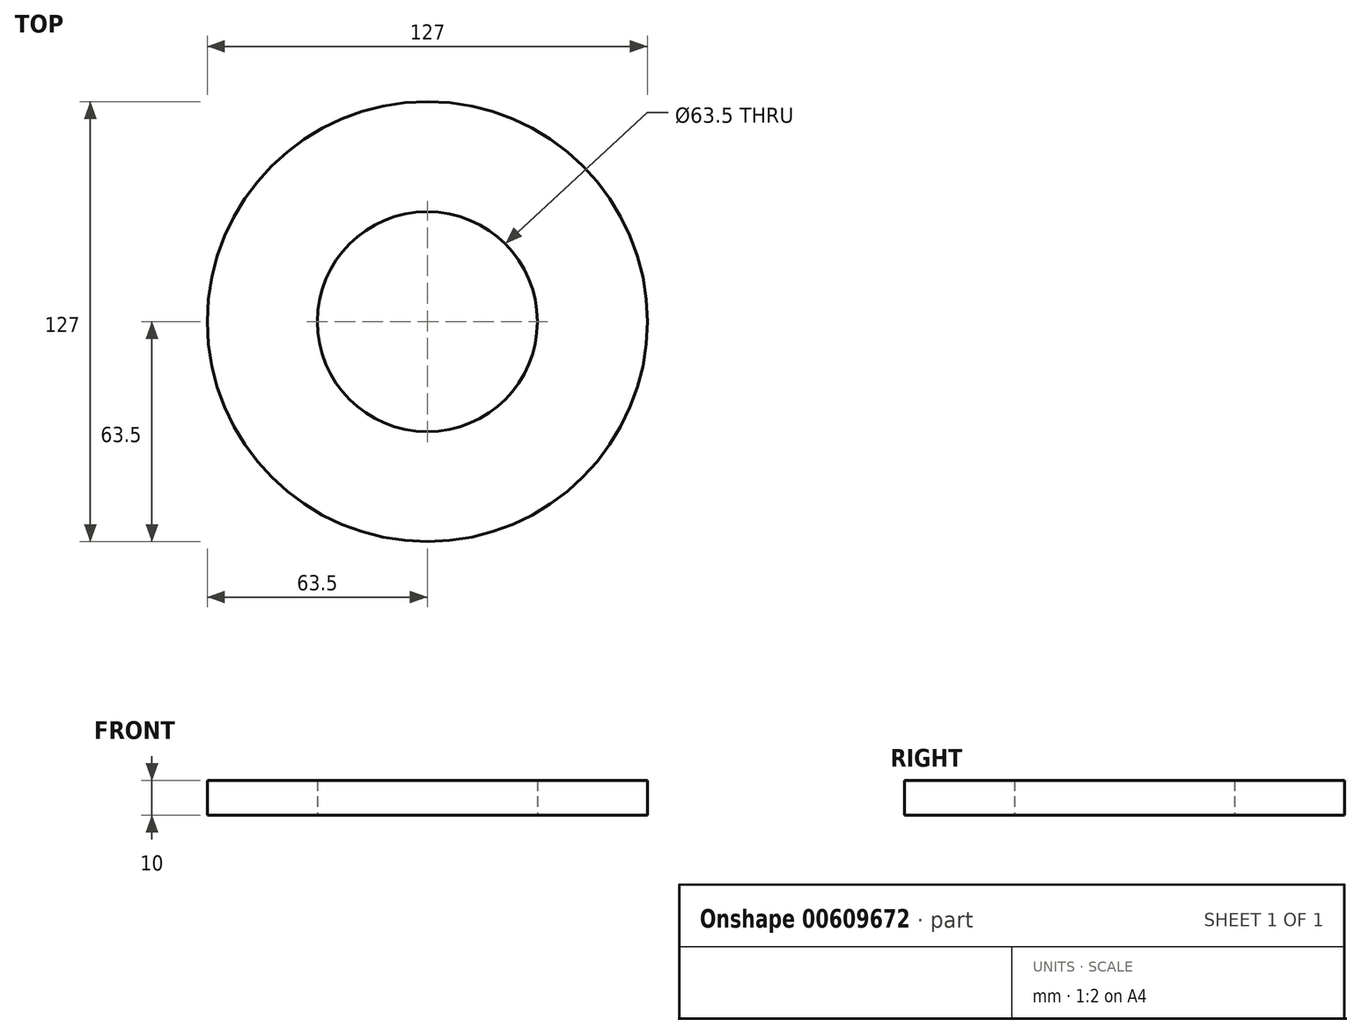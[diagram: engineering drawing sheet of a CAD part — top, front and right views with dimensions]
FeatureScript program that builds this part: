
annotation { "Feature Type Name" : "Feature", "Feature Type Description" : "" }
export const myFeature = defineFeature(function(context is Context, id is Id, definition is map)
    precondition{}
    {
        {
            var Q0;
            Q0=qCreatedBy(makeId("Top.planeOp"),FACE);
            var sketch = newSketch(context, id + "F0", { "sketchPlane" : qUnion([Q0])});
            skCircle(sketch, "E0", {"center": v(0, 0) * mm, "radius": 63.5 * mm});
            skCircle(sketch, "E1", {"center": v(0, 0) * mm, "radius": 31.75 * mm});
            skSolve(sketch);
        }
        {
            var Q0;
            Q0 = qSketchRegion(id + "F0", true);
            extrude(context, id + "F1", {"entities" : qUnion([Q0]), "depth" : 10 * mm, "offsetDistance" : 25.4 * mm});
        }
    });
